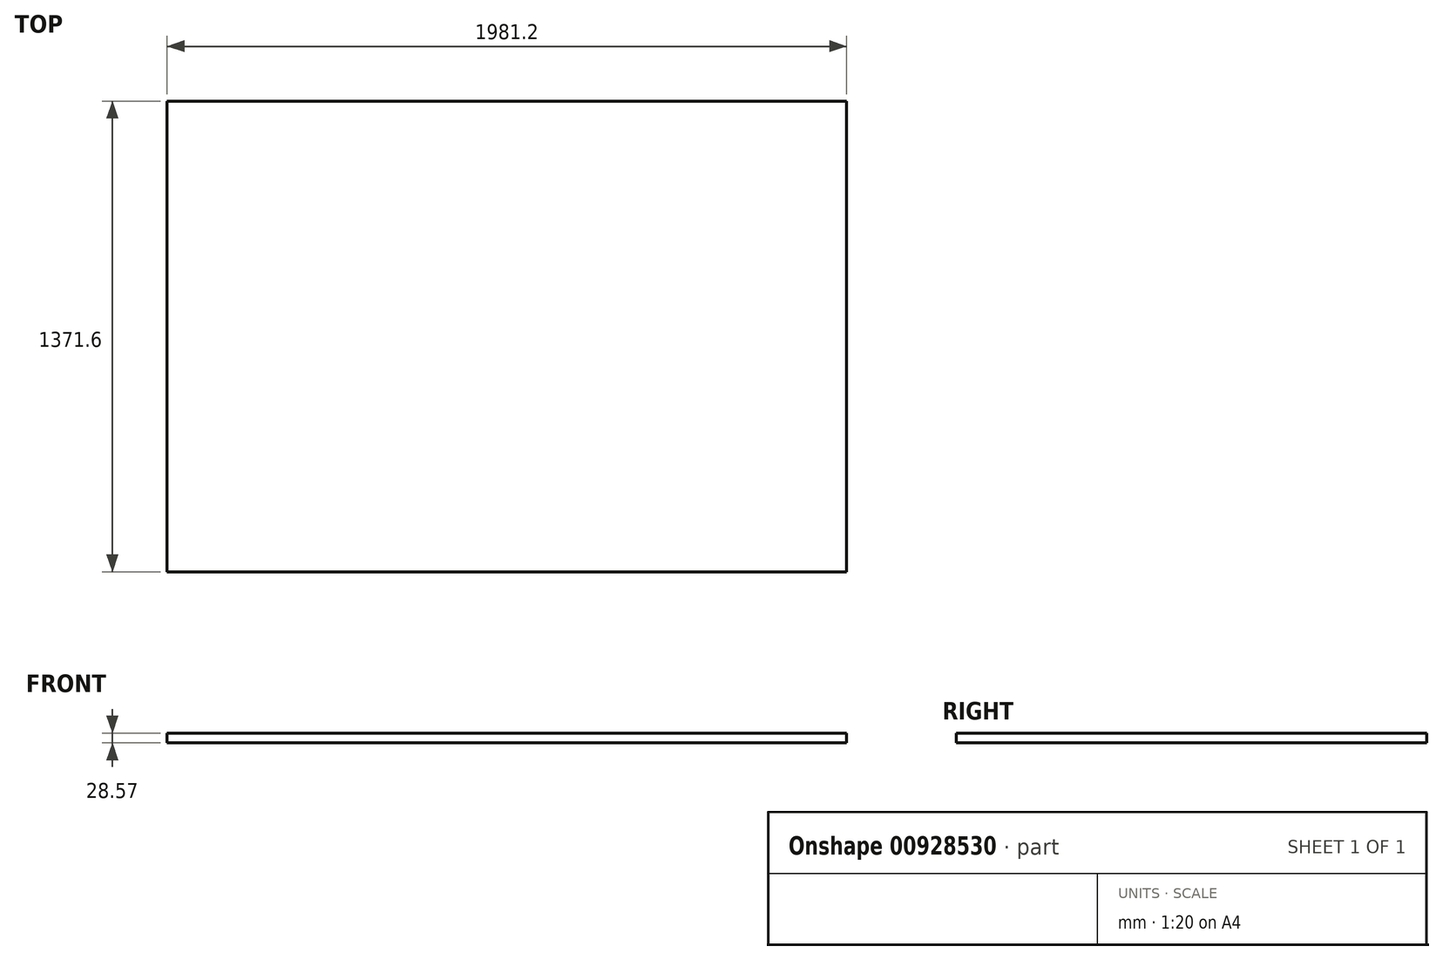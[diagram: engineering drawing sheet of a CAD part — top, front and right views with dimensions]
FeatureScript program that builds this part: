
annotation { "Feature Type Name" : "Feature", "Feature Type Description" : "" }
export const myFeature = defineFeature(function(context is Context, id is Id, definition is map)
    precondition{}
    {
        {
            var Q0;
            Q0=qCreatedBy(makeId("Top.planeOp"),FACE);
            var sketch = newSketch(context, id + "F0", { "sketchPlane" : qUnion([Q0])});
            skLineSegment(sketch, "E0.bottom", {"start": v(990.6, 685.8) * mm, "end": v(-990.6, 685.8) * mm});
            skLineSegment(sketch, "E0.top", {"start": v(990.6, -685.8) * mm, "end": v(-990.6, -685.8) * mm});
            skLineSegment(sketch, "E0.left", {"start": v(990.6, 685.8) * mm, "end": v(990.6, -685.8) * mm});
            skLineSegment(sketch, "E0.right", {"start": v(-990.6, 685.8) * mm, "end": v(-990.6, -685.8) * mm});
            skPoint(sketch, "E0.middle", {"position": v(0, 0) * mm});
            skSolve(sketch);
        }
        {
            var Q0;
            Q0=makeQuery(id+"F0.imprint","IMPRINT",FACE,{"disambiguationData":[TD([[makeQuery(id+"F0.imprint","IMPRINT",EDGE,{"derivedFrom":sQuery(id+"F0.wireOp",EDGE,"E0.bottom")}),1.0]])]});
            extrude(context, id + "F1", {"entities" : qUnion([Q0]), "depth" : 28.57 * mm, "offsetDistance" : 25.4 * mm});
        }
    });
